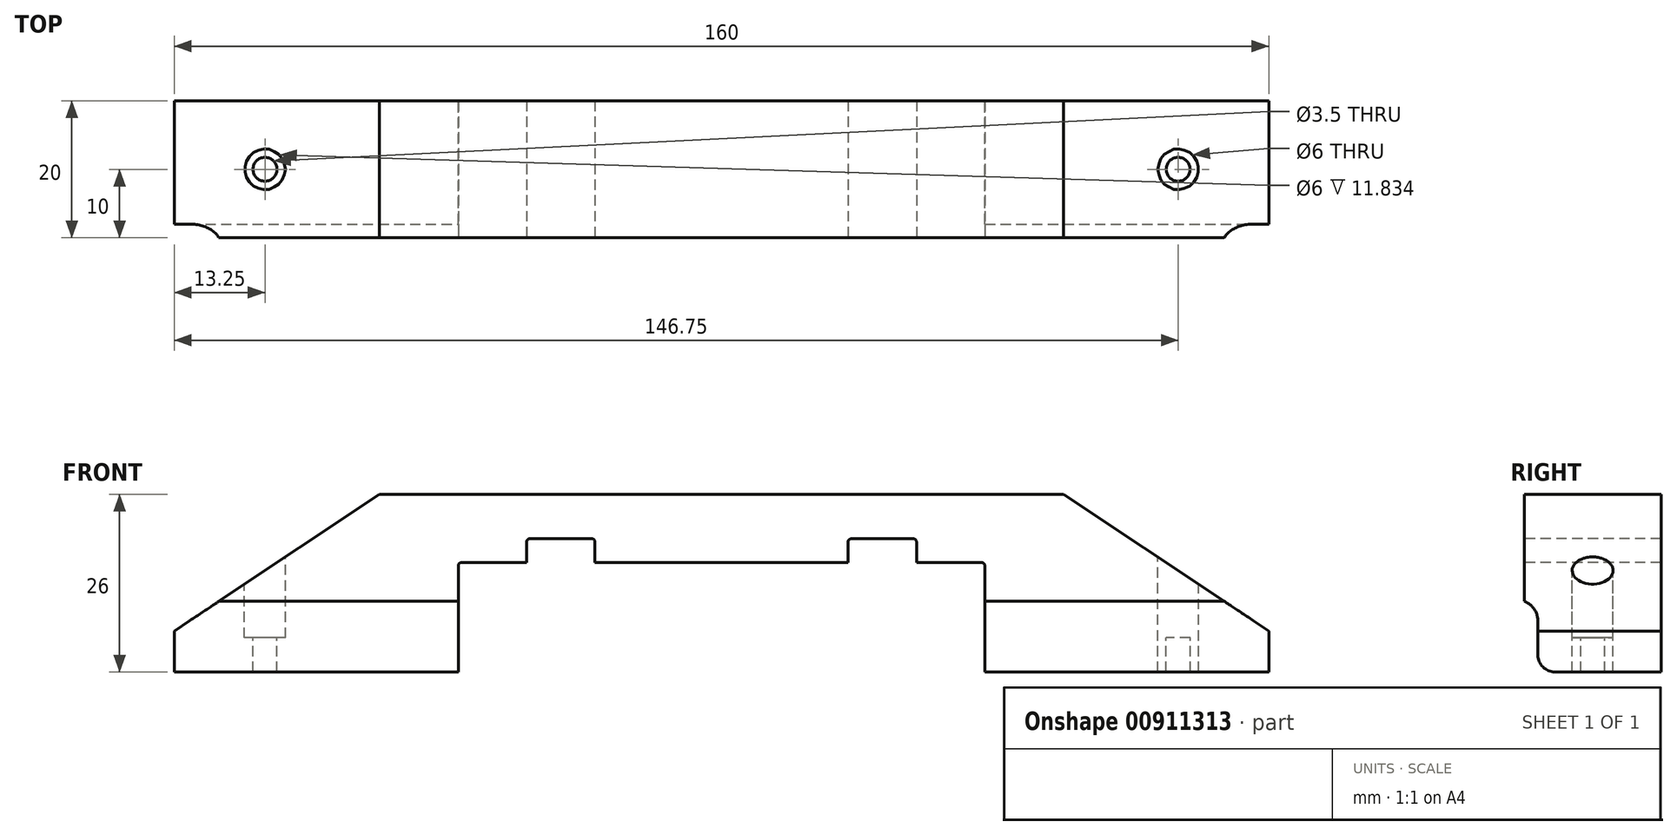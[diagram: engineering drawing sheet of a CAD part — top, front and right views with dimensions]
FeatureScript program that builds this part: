
annotation { "Feature Type Name" : "Feature", "Feature Type Description" : "" }
export const myFeature = defineFeature(function(context is Context, id is Id, definition is map)
    precondition{}
    {
        {
            var Q0;
            Q0=qCreatedBy(makeId("Front.planeOp"),FACE);
            var sketch = newSketch(context, id + "F0", { "sketchPlane" : qUnion([Q0])});
            skLineSegment(sketch, "E0", {"start": v(0, 0) * mm, "end": v(0, -43.5) * mm, "construction": true});
            skLineSegment(sketch, "E1", {"start": v(-43.69, 0) * mm, "end": v(-38.5, 0) * mm, "construction": true});
            skLineSegment(sketch, "E2.0", {"start": v(-38.5, 31) * mm, "end": v(-38.5, -43.5) * mm, "construction": true});
            skLineSegment(sketch, "E3.0", {"start": v(-80, 11) * mm, "end": v(-80, -43.5) * mm, "construction": true});
            skLineSegment(sketch, "E4.0", {"start": v(-43.69, 41) * mm, "end": v(48.56, 41) * mm, "construction": true});
            skLineSegment(sketch, "E5.top", {"start": v(5, 41) * mm, "end": v(-50, 41) * mm});
            skLineSegment(sketch, "E6.top", {"start": v(0, 31) * mm, "end": v(-18.5, 31) * mm});
            skLineSegment(sketch, "E6.right", {"start": v(-38.5, 5) * mm, "end": v(-38.5, 30.5) * mm});
            skLineSegment(sketch, "E7.top", {"start": v(-19, 34.5) * mm, "end": v(-28, 34.5) * mm});
            skLineSegment(sketch, "E7.left", {"start": v(-18.5, 31) * mm, "end": v(-18.5, 34) * mm});
            skLineSegment(sketch, "E7.right", {"start": v(-28.5, 31) * mm, "end": v(-28.5, 34) * mm});
            skPoint(sketch, "E8.orphan", {"position": v(0, 24.75) * mm});
            skLineSegment(sketch, "E9.trimOffspring", {"start": v(-28.5, 31) * mm, "end": v(-38, 31) * mm});
            skLineSegment(sketch, "E10.MirrorCS", {"start": v(-5, 41) * mm, "end": v(50, 41) * mm});
            skLineSegment(sketch, "E11.MirrorCS", {"start": v(0, 31) * mm, "end": v(18.5, 31) * mm});
            skLineSegment(sketch, "E12.MirrorCS", {"start": v(19, 34.5) * mm, "end": v(28, 34.5) * mm});
            skLineSegment(sketch, "E13.MirrorCS", {"start": v(18.5, 31) * mm, "end": v(18.5, 34) * mm});
            skLineSegment(sketch, "E14.MirrorCS", {"start": v(28.5, 31) * mm, "end": v(28.5, 34) * mm});
            skLineSegment(sketch, "E15.MirrorCS", {"start": v(38.5, 5) * mm, "end": v(38.5, 30.5) * mm});
            skLineSegment(sketch, "E16.MirrorCS", {"start": v(28.5, 31) * mm, "end": v(38, 31) * mm});
            skLineSegment(sketch, "E17.trimOffspring", {"start": v(0, 0) * mm, "end": v(48.56, 0) * mm, "construction": true});
            skPoint(sketch, "E18.visualSharp", {"position": v(-28.5, 34.5) * mm});
            skArc(sketch, "E18.filletArc", {"start": v(-28, 34.5) * mm, "mid": v(-28.35, 34.35) * mm, "end": v(-28.5, 34) * mm});
            skPoint(sketch, "E19.visualSharp", {"position": v(-38.5, 31) * mm});
            skArc(sketch, "E19.filletArc", {"start": v(-38, 31) * mm, "mid": v(-38.35, 30.85) * mm, "end": v(-38.5, 30.5) * mm});
            skPoint(sketch, "E20.visualSharp", {"position": v(-18.5, 34.5) * mm});
            skArc(sketch, "E20.filletArc", {"start": v(-18.5, 34) * mm, "mid": v(-18.65, 34.35) * mm, "end": v(-19, 34.5) * mm});
            skPoint(sketch, "E21.visualSharp", {"position": v(18.5, 34.5) * mm});
            skArc(sketch, "E21.filletArc", {"start": v(19, 34.5) * mm, "mid": v(18.65, 34.35) * mm, "end": v(18.5, 34) * mm});
            skPoint(sketch, "E22.visualSharp", {"position": v(28.5, 34.5) * mm});
            skArc(sketch, "E22.filletArc", {"start": v(28.5, 34) * mm, "mid": v(28.35, 34.35) * mm, "end": v(28, 34.5) * mm});
            skPoint(sketch, "E23.visualSharp", {"position": v(38.5, 31) * mm});
            skArc(sketch, "E23.filletArc", {"start": v(38.5, 30.5) * mm, "mid": v(38.35, 30.85) * mm, "end": v(38, 31) * mm});
            skLineSegment(sketch, "E24", {"start": v(-80, 21) * mm, "end": v(-50, 41) * mm});
            skLineSegment(sketch, "E25", {"start": v(-80, 21) * mm, "end": v(-80, 5) * mm});
            skLineSegment(sketch, "E26.MirrorCS", {"start": v(80, 21) * mm, "end": v(50, 41) * mm});
            skLineSegment(sketch, "E27.MirrorCS", {"start": v(80, 21) * mm, "end": v(80, 5) * mm});
            skLineSegment(sketch, "E28.0", {"start": v(-80, 5) * mm, "end": v(-38.5, 5) * mm});
            skPoint(sketch, "E29.orphan", {"position": v(-80, 0) * mm});
            skPoint(sketch, "E30.orphan", {"position": v(38.5, 0) * mm});
            skPoint(sketch, "E31.MirrorCS.end.orphan", {"position": v(80, 0) * mm});
            skLineSegment(sketch, "E32.trimOffspring", {"start": v(38.5, 5) * mm, "end": v(80, 5) * mm});
            skSolve(sketch);
        }
        {
            var Q0;
            Q0=makeQuery(id+"F0.imprint","IMPRINT",FACE,{"disambiguationData":[TD([[makeQuery(id+"F0.imprint","IMPRINT",EDGE,{"derivedFrom":sQuery(id+"F0.wireOp",EDGE,"E5.top")}),1.0]])]});
            extrude(context, id + "F1", {"entities" : qUnion([Q0]), "oppositeDirection" : true, "depth" : 20 * mm, "offsetDistance" : 25 * mm});
        }
        {
            var Q0;
            Q0=qCreatedBy(makeId("Top.planeOp"),FACE);
            cPlane(context, id + "F2", {"entities" : qUnion([Q0]), "cplaneType" : CPlaneType.OFFSET, "offset" : 45 * mm, "width" : 150 * mm, "height" : 150 * mm});
        }
        {
            var Q0;
            Q0=qCreatedBy(id+"F2.planeOp",FACE);
            var sketch = newSketch(context, id + "F3", { "sketchPlane" : qUnion([Q0])});
            skLineSegment(sketch, "E33", {"start": v(0, 0) * mm, "end": v(-136.35, 0) * mm, "construction": true});
            skLineSegment(sketch, "E34", {"start": v(0, 0) * mm, "end": v(0, 2.9) * mm, "construction": true});
            skLineSegment(sketch, "E35", {"start": v(0, 0) * mm, "end": v(0, 42.59) * mm, "construction": true});
            skLineSegment(sketch, "E36.0", {"start": v(-66.75, 0) * mm, "end": v(-66.75, 42.59) * mm, "construction": true});
            skLineSegment(sketch, "E37.0", {"start": v(0, 10) * mm, "end": v(-136.35, 10) * mm, "construction": true});
            skCircle(sketch, "E38", {"center": v(-66.75, 10) * mm, "radius": 1.75 * mm});
            skPoint(sketch, "E38.centerSnap0", {"position": v(-68.18, 10) * mm});
            skCircle(sketch, "E39", {"center": v(-66.75, 10) * mm, "radius": 3 * mm});
            skCircle(sketch, "E40.MirrorC", {"center": v(66.75, 10) * mm, "radius": 1.75 * mm});
            skCircle(sketch, "E41.MirrorC", {"center": v(66.75, 10) * mm, "radius": 3 * mm});
            skSolve(sketch);
        }
        {
            var Q0;
            Q0=makeQuery(id+"F3.imprint","IMPRINT",FACE,{"disambiguationData":[TD([[makeQuery(id+"F3.imprint","IMPRINT",EDGE,{"derivedFrom":sQuery(id+"F3.wireOp",EDGE,"E38")}),1.0]])]});
            var Q1;
            Q1=makeQuery(id+"F3.imprint","IMPRINT",FACE,{"disambiguationData":[TD([[makeQuery(id+"F3.imprint","IMPRINT",EDGE,{"derivedFrom":sQuery(id+"F3.wireOp",EDGE,"E40.MirrorC")}),-1.0]])]});
            extrude(context, id + "F4", {"entities" : qUnion([Q0, Q1]), "operationType" : NewBodyOperationType.REMOVE, "endBound" : BoundingType.THROUGH_ALL, "oppositeDirection" : true, "depth" : 25 * mm, "offsetDistance" : 25 * mm});
        }
        {
            var Q0;
            Q0=makeQuery(id+"F3.imprint","IMPRINT",FACE,{"disambiguationData":[TD([[makeQuery(id+"F3.imprint","IMPRINT",EDGE,{"derivedFrom":sQuery(id+"F3.wireOp",EDGE,"E38")}),-1.0]])]});
            var Q1;
            Q1=makeQuery(id+"F3.imprint","IMPRINT",FACE,{"disambiguationData":[TD([[makeQuery(id+"F3.imprint","IMPRINT",EDGE,{"derivedFrom":sQuery(id+"F3.wireOp",EDGE,"E40.MirrorC")}),1.0]])]});
            extrude(context, id + "F5", {"entities" : qUnion([Q0, Q1]), "operationType" : NewBodyOperationType.REMOVE, "oppositeDirection" : true, "depth" : 25 * mm, "offsetDistance" : 25 * mm});
        }
        {
            var Q0;
            Q0=qCreatedBy(makeId("Front.planeOp"),FACE);
            var sketch = newSketch(context, id + "F6", { "sketchPlane" : qUnion([Q0])});
            skLineSegment(sketch, "E42.bottom", {"start": v(-80, 5) * mm, "end": v(80, 5) * mm});
            skLineSegment(sketch, "E42.top", {"start": v(-80, 15) * mm, "end": v(80, 15) * mm});
            skLineSegment(sketch, "E42.left", {"start": v(-80, 5) * mm, "end": v(-80, 15) * mm});
            skLineSegment(sketch, "E42.right", {"start": v(80, 5) * mm, "end": v(80, 15) * mm});
            skSolve(sketch);
        }
        {
            var Q0;
            Q0 = qSketchRegion(id + "F6", true);
            extrude(context, id + "F7", {"entities" : qUnion([Q0]), "operationType" : NewBodyOperationType.REMOVE, "endBound" : BoundingType.THROUGH_ALL, "oppositeDirection" : true, "depth" : 25 * mm, "offsetDistance" : 25 * mm});
        }
        {
            var Q0;
            Q0=qCreatedBy(makeId("Right.planeOp"),FACE);
            var sketch = newSketch(context, id + "F8", { "sketchPlane" : qUnion([Q0])});
            skLineSegment(sketch, "E43", {"start": v(20, 15) * mm, "end": v(20, 53.2) * mm, "construction": true});
            skPoint(sketch, "E44.visualSharp", {"position": v(1.5, 25) * mm});
            skPoint(sketch, "E45.visualSharp", {"position": v(-8.5, 25) * mm});
            skLineSegment(sketch, "E46", {"start": v(4.5, 15) * mm, "end": v(20, 15) * mm});
            skLineSegment(sketch, "E47.0", {"start": v(2, 17.5) * mm, "end": v(1.99, 22.5) * mm});
            skArc(sketch, "E47.3", {"start": v(1.99, 22.5) * mm, "mid": v(1.44, 24.23) * mm, "end": v(0, 25.33) * mm});
            skLineSegment(sketch, "E48", {"start": v(2, 15) * mm, "end": v(20, 15) * mm});
            skArc(sketch, "E49.filletArc", {"start": v(2, 17.5) * mm, "mid": v(2.73, 15.73) * mm, "end": v(4.5, 15) * mm});
            skLineSegment(sketch, "E50", {"start": v(0, 25.33) * mm, "end": v(0, 15) * mm});
            skLineSegment(sketch, "E51", {"start": v(0, 15) * mm, "end": v(4.5, 15) * mm});
            skSolve(sketch);
        }
        {
            var Q0;
            Q0 = qSketchRegion(id + "F8", true);
            extrude(context, id + "F9", {"entities" : qUnion([Q0]), "operationType" : NewBodyOperationType.REMOVE, "endBound" : BoundingType.THROUGH_ALL, "oppositeDirection" : true, "depth" : 25 * mm, "offsetDistance" : 25 * mm, "hasSecondDirection" : true, "secondDirectionBound" : SecondDirectionBoundingType.THROUGH_ALL, "secondDirectionOppositeDirection" : false, "secondDirectionDepth" : 25 * mm});
        }
    });
